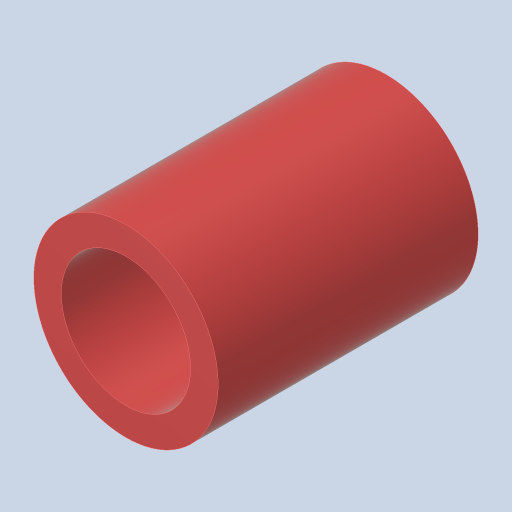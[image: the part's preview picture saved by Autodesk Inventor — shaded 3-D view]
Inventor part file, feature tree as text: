
AUTODESK INVENTOR PART (.ipt)
format: ipt  version: 2023.4 (Build 274418000, 418)  size: 119,808 bytes
history: native  units: in
note: dims shown in document units (in); Inventor stores cm internally (conversion verified against a paired STEP export)
features: extrude x1, sketch x1
ambient origin geometry x8: Origin, YZ Plane, XZ Plane, XY Plane, X Axis, Y Axis, Z Axis, Center Point
bodies: Solid1 (feature_tree)
feature tree (2):
  extrude  "Extrusion1"  Depth=1.178in
  sketch  "Sketch1"  dims[d0=0.585in d1=0.125in d2=1.178in d3=0.0in]
